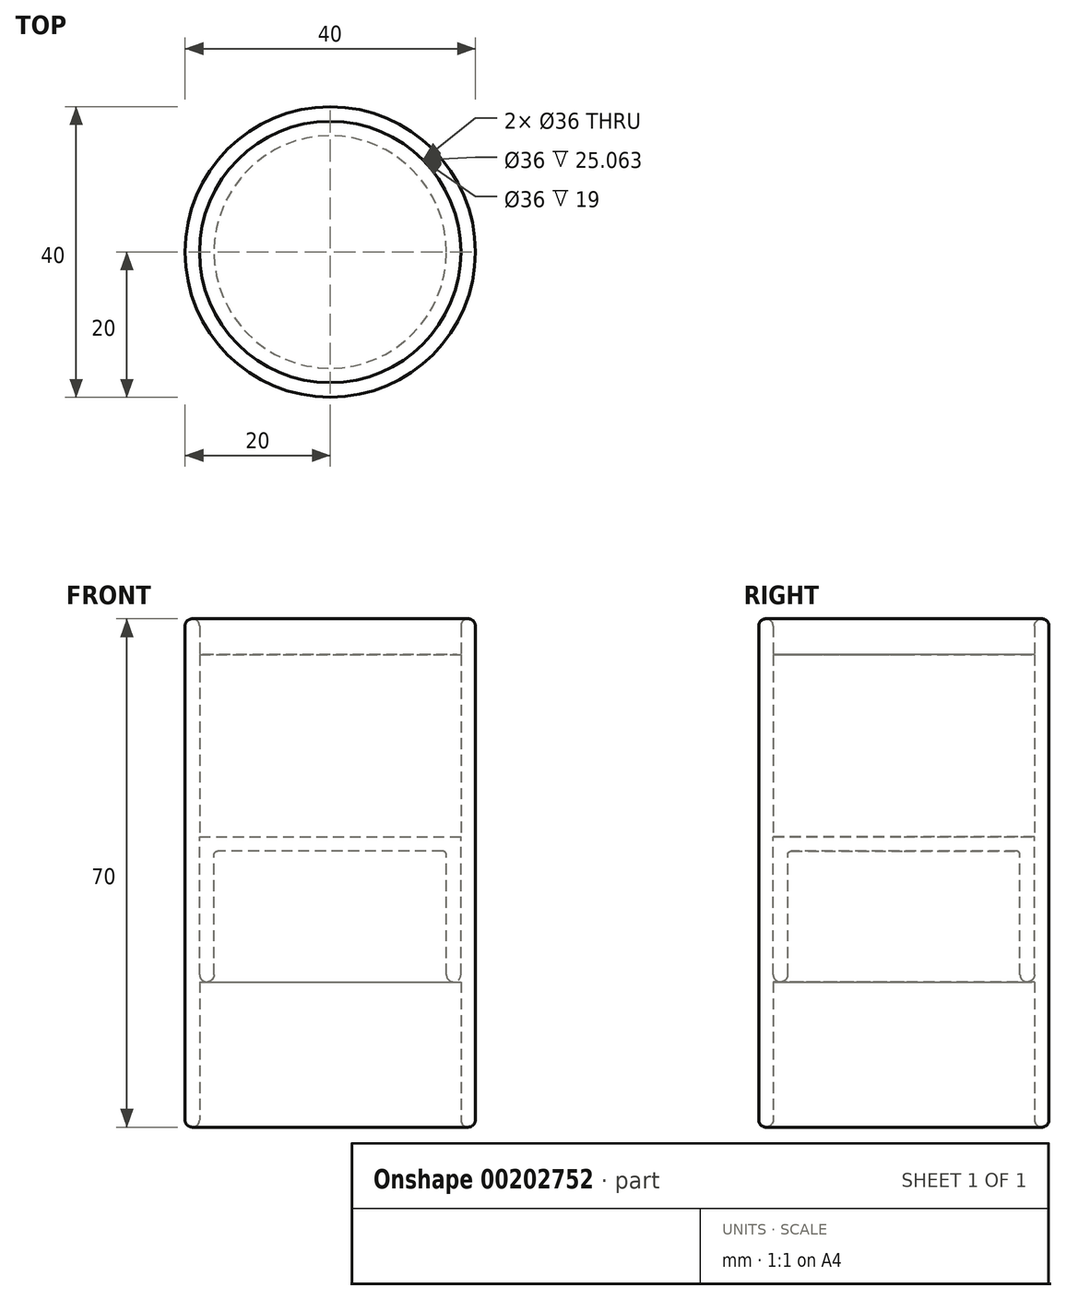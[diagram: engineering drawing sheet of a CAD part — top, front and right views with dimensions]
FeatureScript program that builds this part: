
annotation { "Feature Type Name" : "Feature", "Feature Type Description" : "" }
export const myFeature = defineFeature(function(context is Context, id is Id, definition is map)
    precondition{}
    {
        {
            var Q0;
            Q0=qCreatedBy(makeId("Front.planeOp"),FACE);
            var sketch = newSketch(context, id + "F0", { "sketchPlane" : qUnion([Q0])});
            skLineSegment(sketch, "E0", {"start": v(0, 0) * mm, "end": v(0, 70) * mm});
            skLineSegment(sketch, "E1", {"start": v(0, 70) * mm, "end": v(2, 70) * mm});
            skLineSegment(sketch, "E2", {"start": v(2, 70) * mm, "end": v(2, 65.06) * mm});
            skLineSegment(sketch, "E3", {"start": v(0, 0) * mm, "end": v(2, 0) * mm});
            skLineSegment(sketch, "E4", {"start": v(2, 0) * mm, "end": v(2, 20) * mm});
            skLineSegment(sketch, "E5", {"start": v(0, 35) * mm, "end": v(20, 35) * mm, "construction": true});
            skLineSegment(sketch, "E6", {"start": v(20, 47.4) * mm, "end": v(20, 26.2) * mm, "construction": true});
            skSolve(sketch);
        }
        {
            var Q0;
            Q0=sQuery(id+"F0.wireOp",EDGE,"E6");
            var Q1;
            Q1=sQuery(id+"F0.wireOp",EDGE,"E2");
            var Q2;
            Q2=sQuery(id+"F0.wireOp",EDGE,"E1");
            var Q3;
            Q3=sQuery(id+"F0.wireOp",EDGE,"E0");
            var Q4;
            Q4=sQuery(id+"F0.wireOp",EDGE,"E3");
            var Q5;
            Q5=sQuery(id+"F0.wireOp",EDGE,"E4");
            var Q6;
            Q6 = qConstructionFilter(qBodyType(qCreatedBy(id + "F2" ,EDGE), BodyType.WIRE), ConstructionObject.NO);
            var Q7;
            Q7=sQuery(id+"F0.wireOp",EDGE,"E6");
            revolve(context, id + "F1", {"bodyType" : ToolBodyType.SURFACE, "surfaceEntities" : qUnion([Q0, Q1, Q2, Q3, Q4, Q5, Q6]), "axis" : qUnion([Q7]), "revolveType" : RevolveType.FULL});
        }
        {
            var Q0;
            Q0=qCreatedBy(makeId("Front.planeOp"),FACE);
            var sketch = newSketch(context, id + "F2", { "sketchPlane" : qUnion([Q0])});
            skLineSegment(sketch, "E7.0", {"start": v(2, 20) * mm, "end": v(38, 20) * mm});
            skLineSegment(sketch, "E8", {"start": v(2, 20) * mm, "end": v(2, 40) * mm});
            skLineSegment(sketch, "E9", {"start": v(20, 20) * mm, "end": v(20, 40) * mm});
            skLineSegment(sketch, "E10", {"start": v(20, 40) * mm, "end": v(2, 40) * mm});
            skLineSegment(sketch, "E11.0", {"start": v(20, 38) * mm, "end": v(4, 38) * mm});
            skLineSegment(sketch, "E11.1", {"start": v(4, 20) * mm, "end": v(4, 38) * mm});
            skLineSegment(sketch, "E12", {"start": v(4, 20) * mm, "end": v(2, 20) * mm});
            skSolve(sketch);
        }
        {
            var Q0;
            Q0 = qSketchRegion(id + "F2", true);
            var Q1;
            Q1=sQuery(id+"F2.wireOp",EDGE,"E8");
            var Q2;
            Q2=sQuery(id+"F2.wireOp",EDGE,"E11.1");
            var Q3;
            Q3=sQuery(id+"F2.wireOp",EDGE,"E11.0");
            var Q4;
            Q4=sQuery(id+"F2.wireOp",EDGE,"E10");
            var Q5;
            Q5=sQuery(id+"F2.wireOp",EDGE,"E12");
            var Q6;
            Q6=sQuery(id+"F2.wireOp",EDGE,"E9");
            revolve(context, id + "F3", {"bodyType" : ToolBodyType.SURFACE, "entities" : qUnion([Q0]), "surfaceEntities" : qUnion([Q1, Q2, Q3, Q4, Q5]), "axis" : qUnion([Q6]), "revolveType" : RevolveType.FULL});
        }
        {
            var Q0;
            Q0=qCreatedBy(makeId("Front.planeOp"),FACE);
            var sketch = newSketch(context, id + "F4", { "sketchPlane" : qUnion([Q0])});
            skLineSegment(sketch, "E13.0", {"start": v(2, 40) * mm, "end": v(20, 40) * mm});
            skLineSegment(sketch, "E14", {"start": v(2, 65.06) * mm, "end": v(2, 40) * mm});
            skLineSegment(sketch, "E15", {"start": v(20, 65.06) * mm, "end": v(20, 40) * mm});
            skPoint(sketch, "E16.orphan", {"position": v(38, 65.06) * mm});
            skPoint(sketch, "E17.orphan", {"position": v(38, 40) * mm});
            skSolve(sketch);
        }
        {
            var Q0;
            Q0 = qSketchRegion(id + "F4", true);
            var Q1;
            Q1=sQuery(id+"F4.wireOp",EDGE,"E14");
            var Q2;
            Q2=sQuery(id+"F4.wireOp",EDGE,"E13.0");
            var Q3;
            Q3=sQuery(id+"F4.wireOp",EDGE,"E15");
            revolve(context, id + "F5", {"bodyType" : ToolBodyType.SURFACE, "entities" : qUnion([Q0]), "surfaceEntities" : qUnion([Q1, Q2]), "axis" : qUnion([Q3]), "revolveType" : RevolveType.FULL});
        }
        {
            var Q0;
            Q0=qCreatedBy(makeId("Front.planeOp"),FACE);
            var sketch = newSketch(context, id + "F6", { "sketchPlane" : qUnion([Q0])});
            skLineSegment(sketch, "E18.0", {"start": v(20, 65.06) * mm, "end": v(2, 65.06) * mm});
            skLineSegment(sketch, "E19", {"start": v(20, 65.06) * mm, "end": v(20, 54.77) * mm});
            skPoint(sketch, "E20.orphan", {"position": v(38, 65.06) * mm});
            skSolve(sketch);
        }
        {
            var Q0;
            Q0 = qSketchRegion(id + "F6", true);
            var Q1;
            Q1=sQuery(id+"F6.wireOp",EDGE,"E18.0");
            var Q2;
            Q2=sQuery(id+"F6.wireOp",EDGE,"E19");
            revolve(context, id + "F7", {"bodyType" : ToolBodyType.SURFACE, "entities" : qUnion([Q0]), "surfaceEntities" : qUnion([Q1]), "axis" : qUnion([Q2]), "revolveType" : RevolveType.FULL});
        }
        {
            var Q0;
            Q0=makeQuery(id+"F3.opRevolve","SWEPT_FACE",FACE,{"disambiguationData":[OSD([sQuery(id+"F2.wireOp",EDGE,"E12")])]});
            fillet(context, id + "F8", {"entities" : qUnion([Q0]), "radius" : 1 * mm, "tangentPropagation" : true, "allowEdgeOverflow" : false});
        }
        {
            var Q0;
            Q0=makeQuery(id+"F3.opRevolve","SWEPT_EDGE",EDGE,{"disambiguationData":[OSD([sQuery(id+"F2.wireOp",VERTEX,"E11.0.end")])]});
            fillet(context, id + "F9", {"entities" : qUnion([Q0]), "radius" : 0.5 * mm, "tangentPropagation" : true, "allowEdgeOverflow" : false});
        }
        {
            var Q0;
            Q0=makeQuery(id+"F1.opRevolve","SWEPT_FACE",FACE,{"disambiguationData":[OSD([sQuery(id+"F0.wireOp",EDGE,"E1")])]});
            var Q1;
            Q1=makeQuery(id+"F1.opRevolve","SWEPT_FACE",FACE,{"disambiguationData":[OSD([sQuery(id+"F0.wireOp",EDGE,"E3")])]});
            fillet(context, id + "F10", {"entities" : qUnion([Q0, Q1]), "radius" : 1 * mm, "tangentPropagation" : true, "allowEdgeOverflow" : false});
        }
    });
